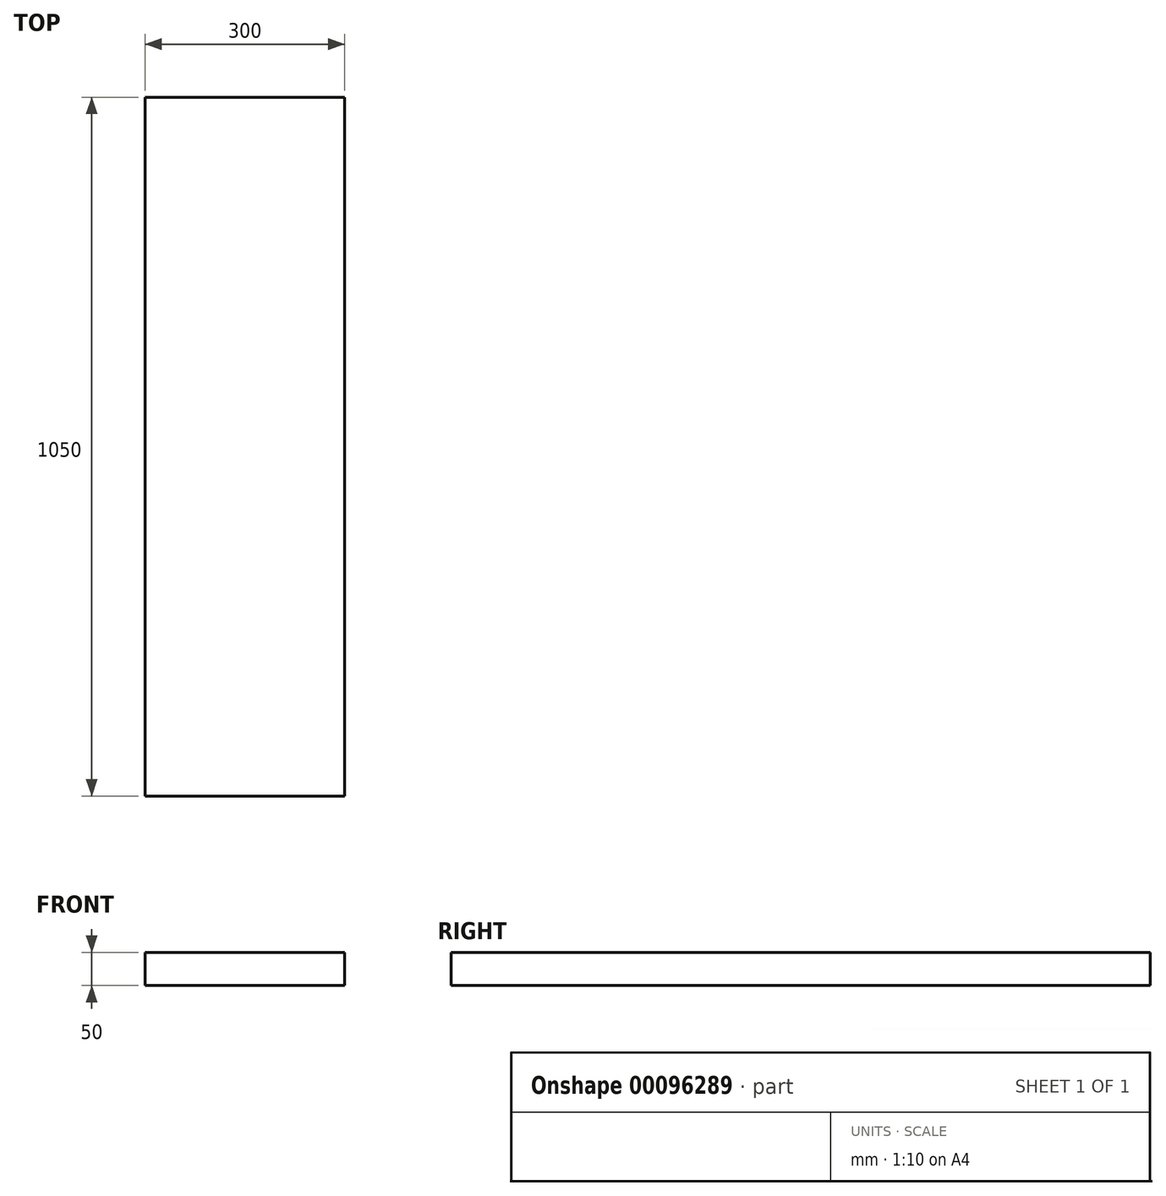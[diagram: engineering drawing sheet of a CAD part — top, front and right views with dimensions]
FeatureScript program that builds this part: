
annotation { "Feature Type Name" : "Feature", "Feature Type Description" : "" }
export const myFeature = defineFeature(function(context is Context, id is Id, definition is map)
    precondition{}
    {
        {
            var Q0;
            Q0=qCreatedBy(makeId("Top.planeOp"),FACE);
            var sketch = newSketch(context, id + "F0", { "sketchPlane" : qUnion([Q0])});
            skLineSegment(sketch, "E0.bottom", {"start": v(-150, 525) * mm, "end": v(150, 525) * mm});
            skLineSegment(sketch, "E0.top", {"start": v(-150, -525) * mm, "end": v(150, -525) * mm});
            skLineSegment(sketch, "E0.left", {"start": v(-150, 525) * mm, "end": v(-150, -525) * mm});
            skLineSegment(sketch, "E0.right", {"start": v(150, 525) * mm, "end": v(150, -525) * mm});
            skPoint(sketch, "E0.middle", {"position": v(0, 0) * mm});
            skSolve(sketch);
        }
        {
            var Q0;
            Q0=makeQuery(id+"F0.imprint","IMPRINT",FACE,{"disambiguationData":[TD([[makeQuery(id+"F0.imprint","IMPRINT",EDGE,{"derivedFrom":sQuery(id+"F0.wireOp",EDGE,"E0.bottom")}),-1.0]])]});
            extrude(context, id + "F1", {"entities" : qUnion([Q0]), "endBound" : BoundingType.SYMMETRIC, "depth" : 50 * mm});
        }
    });
